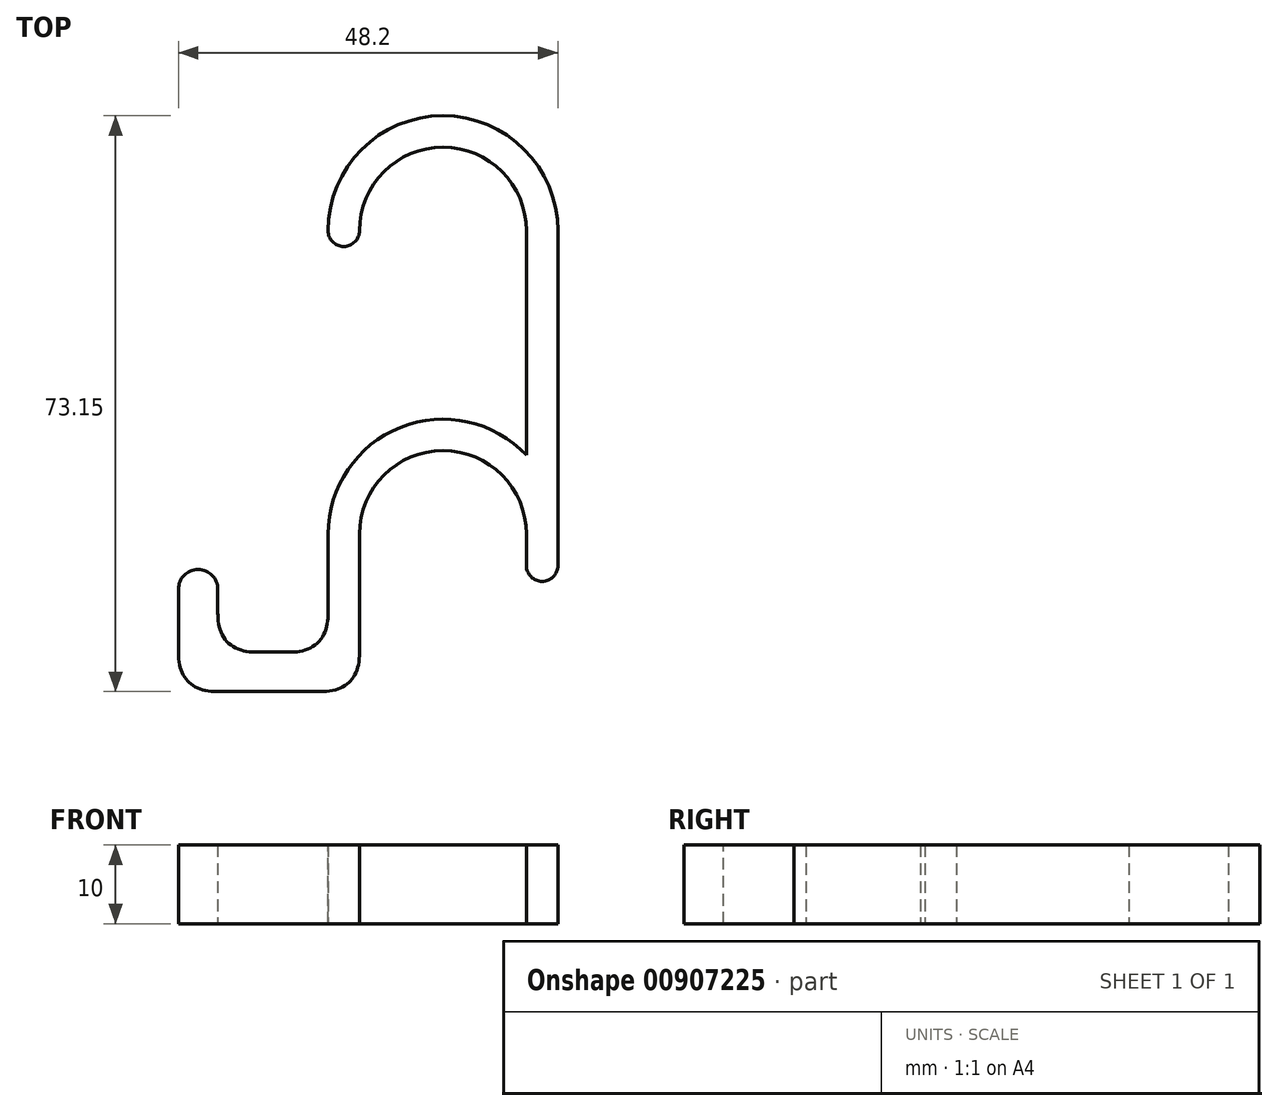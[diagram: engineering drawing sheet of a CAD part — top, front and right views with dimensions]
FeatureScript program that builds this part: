
annotation { "Feature Type Name" : "Feature", "Feature Type Description" : "" }
export const myFeature = defineFeature(function(context is Context, id is Id, definition is map)
    precondition{}
    {
        {
            var Q0;
            Q0=qCreatedBy(makeId("Top.planeOp"),FACE);
            var sketch = newSketch(context, id + "F0", { "sketchPlane" : qUnion([Q0])});
            skLineSegment(sketch, "E0", {"start": v(14.6, 38.55) * mm, "end": v(14.6, -4) * mm});
            skLineSegment(sketch, "E1", {"start": v(10.6, -4) * mm, "end": v(10.6, 0) * mm});
            skLineSegment(sketch, "E2", {"start": v(-33.6, -7) * mm, "end": v(-33.6, -20) * mm});
            skLineSegment(sketch, "E3", {"start": v(-33.6, -20) * mm, "end": v(-10.6, -20) * mm});
            skLineSegment(sketch, "E4", {"start": v(-10.6, -20) * mm, "end": v(-10.6, 0) * mm});
            skLineSegment(sketch, "E5", {"start": v(-14.6, 0) * mm, "end": v(-14.6, -15) * mm});
            skLineSegment(sketch, "E6", {"start": v(-14.6, -15) * mm, "end": v(-28.6, -15) * mm});
            skLineSegment(sketch, "E7", {"start": v(-28.6, -15) * mm, "end": v(-28.6, -7) * mm});
            skLineSegment(sketch, "E8", {"start": v(-33.6, -7) * mm, "end": v(-28.6, -7) * mm, "construction": true});
            skLineSegment(sketch, "E9", {"start": v(10.6, 10.04) * mm, "end": v(10.6, 38.55) * mm});
            skCircle(sketch, "E10", {"center": v(0, 38.55) * mm, "radius": 10.25 * mm, "construction": true});
            skCircle(sketch, "E11", {"center": v(0, 0) * mm, "radius": 10.25 * mm, "construction": true});
            skLineSegment(sketch, "E12", {"start": v(0, 38.55) * mm, "end": v(0, 0) * mm, "construction": true});
            skArc(sketch, "E13", {"start": v(-10.6, 38.55) * mm, "mid": v(0, 49.15) * mm, "end": v(10.6, 38.55) * mm});
            skArc(sketch, "E14", {"start": v(-14.6, 38.55) * mm, "mid": v(0, 53.15) * mm, "end": v(14.6, 38.55) * mm});
            skArc(sketch, "E15", {"start": v(-14.6, 38.55) * mm, "mid": v(-12.6, 36.55) * mm, "end": v(-10.6, 38.55) * mm});
            skArc(sketch, "E16", {"start": v(-10.6, 0) * mm, "mid": v(0, 10.6) * mm, "end": v(10.6, 0) * mm});
            skArc(sketch, "E17", {"start": v(-14.6, 0) * mm, "mid": v(-5.4, 13.56) * mm, "end": v(10.6, 10.04) * mm});
            skArc(sketch, "E18", {"start": v(10.6, -4) * mm, "mid": v(12.6, -6) * mm, "end": v(14.6, -4) * mm});
            skLineSegment(sketch, "E19", {"start": v(10.6, -4) * mm, "end": v(14.6, -4) * mm, "construction": true});
            skArc(sketch, "E20", {"start": v(-33.6, -7) * mm, "mid": v(-31.1, -4.5) * mm, "end": v(-28.6, -7) * mm});
            skSolve(sketch);
        }
        {
            var Q0;
            Q0 = qSketchRegion(id + "F0", true);
            extrude(context, id + "F1", {"entities" : qUnion([Q0]), "depth" : 10 * mm, "offsetDistance" : 25 * mm});
        }
        {
            var Q0;
            Q0=makeQuery(id+"F1.opExtrude","SWEPT_EDGE",EDGE,{"disambiguationData":[OSD([sQuery(id+"F0.wireOp",EDGE,"E5"),sQuery(id+"F0.wireOp",EDGE,"E6")])]});
            var Q1;
            Q1=makeQuery(id+"F1.opExtrude","SWEPT_EDGE",EDGE,{"disambiguationData":[OSD([sQuery(id+"F0.wireOp",EDGE,"E6"),sQuery(id+"F0.wireOp",EDGE,"E7")])]});
            var Q2;
            Q2=makeQuery(id+"F1.opExtrude","SWEPT_EDGE",EDGE,{"disambiguationData":[OSD([sQuery(id+"F0.wireOp",EDGE,"E2"),sQuery(id+"F0.wireOp",EDGE,"E3")])]});
            var Q3;
            Q3=makeQuery(id+"F1.opExtrude","SWEPT_EDGE",EDGE,{"disambiguationData":[OSD([sQuery(id+"F0.wireOp",EDGE,"E3"),sQuery(id+"F0.wireOp",EDGE,"E4")])]});
            fillet(context, id + "F2", {"entities" : qUnion([Q0, Q1, Q2, Q3]), "tangentPropagation" : true, "crossSection" : FilletCrossSection.CONIC, "radius" : 5 * mm, "rho" : 0.5, "defaultsChanged" : false, "vertexSettings" : [], "allowEdgeOverflow" : false});
        }
    });
